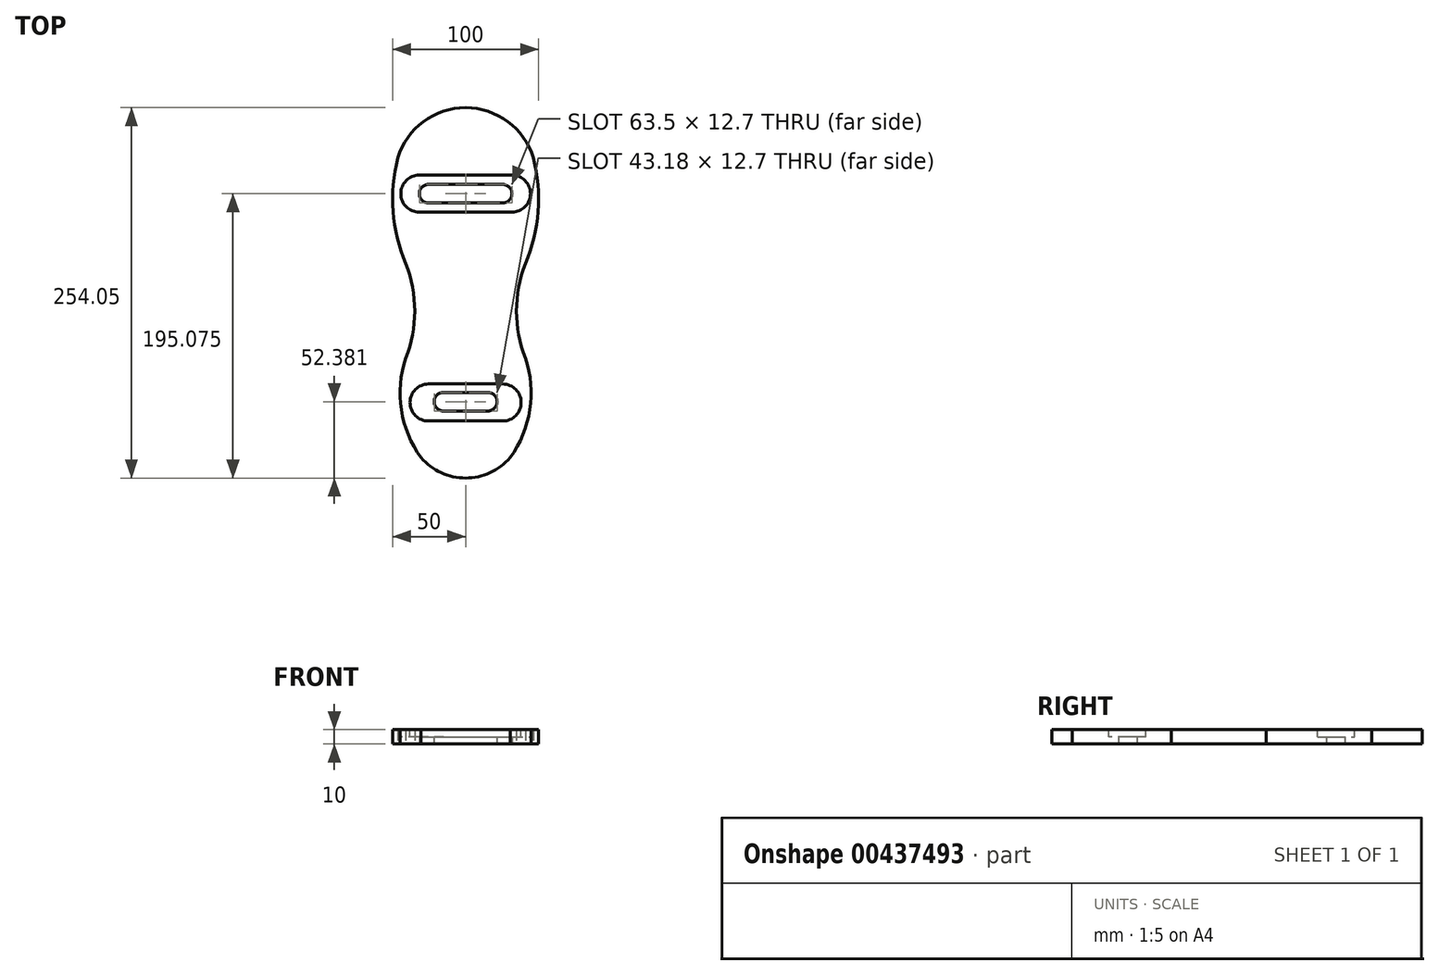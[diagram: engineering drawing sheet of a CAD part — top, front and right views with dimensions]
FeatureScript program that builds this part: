
annotation { "Feature Type Name" : "Feature", "Feature Type Description" : "" }
export const myFeature = defineFeature(function(context is Context, id is Id, definition is map)
    precondition{}
    {
        {
            var Q0;
            Q0=qCreatedBy(makeId("Top.planeOp"),FACE);
            var sketch = newSketch(context, id + "F0", { "sketchPlane" : qUnion([Q0])});
            skArc(sketch, "E0", {"start": v(-46.53, 5.97) * mm, "mid": v(-49.68, -30.66) * mm, "end": v(-41.15, -66.42) * mm});
            skArc(sketch, "E1", {"start": v(-41.15, -131.35) * mm, "mid": v(-34.86, -98.88) * mm, "end": v(-41.15, -66.42) * mm});
            skArc(sketch, "E2", {"start": v(-41.15, -131.35) * mm, "mid": v(-44.1, -166.7) * mm, "end": v(-30.54, -199.47) * mm});
            skLineSegment(sketch, "E3", {"start": v(0, 0) * mm, "end": v(0, -117.28) * mm});
            skArc(sketch, "E4.MirrorCS", {"start": v(46.53, 5.97) * mm, "mid": v(49.68, -30.66) * mm, "end": v(41.15, -66.42) * mm});
            skArc(sketch, "E5.MirrorCS", {"start": v(41.15, -131.35) * mm, "mid": v(34.86, -98.88) * mm, "end": v(41.15, -66.42) * mm});
            skArc(sketch, "E6.MirrorCS", {"start": v(41.15, -131.35) * mm, "mid": v(44.1, -166.7) * mm, "end": v(30.54, -199.47) * mm});
            skArc(sketch, "E7", {"start": v(-30.54, -199.47) * mm, "mid": v(0, -213.5) * mm, "end": v(30.54, -199.47) * mm});
            skArc(sketch, "E8", {"start": v(46.53, 5.97) * mm, "mid": v(0, 40.56) * mm, "end": v(-46.53, 5.97) * mm});
            skSolve(sketch);
        }
        {
            var Q0;
            Q0=makeQuery(id+"F0.imprint","IMPRINT",FACE,{"disambiguationData":[TD([[makeQuery(id+"F0.imprint","IMPRINT",EDGE,{"derivedFrom":sQuery(id+"F0.wireOp",EDGE,"E0")}),1.0]])]});
            extrude(context, id + "F1", {"entities" : qUnion([Q0]), "depth" : 10 * mm});
        }
        {
            var Q0;
            Q0=makeQuery(id+"F1.opExtrude","CAP_FACE",FACE,{"disambiguationData":[OSD([sQuery(id+"F0.wireOp",EDGE,"E0"),sQuery(id+"F0.wireOp",EDGE,"E1"),sQuery(id+"F0.wireOp",EDGE,"E2"),sQuery(id+"F0.wireOp",EDGE,"E4.MirrorCS"),sQuery(id+"F0.wireOp",EDGE,"E5.MirrorCS"),sQuery(id+"F0.wireOp",EDGE,"E6.MirrorCS"),sQuery(id+"F0.wireOp",EDGE,"E7"),sQuery(id+"F0.wireOp",EDGE,"E8")])],"isStart":false});
            var sketch = newSketch(context, id + "F2", { "sketchPlane" : qUnion([Q0])});
            skLineSegment(sketch, "E9", {"start": v(0, 0) * mm, "end": v(0, -18.41) * mm});
            skLineSegment(sketch, "E10", {"start": v(0, -18.41) * mm, "end": v(-31.75, -18.41) * mm});
            skCircle(sketch, "E11", {"center": v(-31.75, -18.41) * mm, "radius": 12.7 * mm});
            skCircle(sketch, "E12.MirrorC", {"center": v(31.75, -18.41) * mm, "radius": 12.7 * mm});
            skLineSegment(sketch, "E13", {"start": v(-31.75, -5.71) * mm, "end": v(31.75, -5.71) * mm});
            skLineSegment(sketch, "E14", {"start": v(31.75, -31.12) * mm, "end": v(-31.75, -31.12) * mm});
            skSolve(sketch);
        }
        {
            var Q0;
            Q0 = qSketchRegion(id + "F2", true);
            extrude(context, id + "F3", {"entities" : qUnion([Q0]), "operationType" : NewBodyOperationType.REMOVE, "oppositeDirection" : true, "depth" : 5 * mm});
        }
        {
            var Q0;
            Q0=makeQuery(id+"F3.boolean.opBoolean","COPY",FACE,{"derivedFrom":makeQuery(id+"F3.opExtrude","CAP_FACE",FACE,{"disambiguationData":[OSD([sQuery(id+"F2.wireOp",EDGE,"E11"),sQuery(id+"F2.wireOp",EDGE,"E12.MirrorC"),sQuery(id+"F2.wireOp",EDGE,"E13"),sQuery(id+"F2.wireOp",EDGE,"E14")])],"isStart":false})});
            var sketch = newSketch(context, id + "F4", { "sketchPlane" : qUnion([Q0])});
            skLineSegment(sketch, "E15", {"start": v(-31.75, -18.41) * mm, "end": v(-31.75, -12.06) * mm});
            skLineSegment(sketch, "E16", {"start": v(-31.75, -12.06) * mm, "end": v(31.75, -12.06) * mm});
            skLineSegment(sketch, "E17", {"start": v(31.75, -12.06) * mm, "end": v(31.75, -24.76) * mm});
            skLineSegment(sketch, "E18", {"start": v(31.75, -24.76) * mm, "end": v(-31.75, -24.76) * mm});
            skLineSegment(sketch, "E19", {"start": v(-31.75, -24.76) * mm, "end": v(-31.75, -18.41) * mm});
            skSolve(sketch);
        }
        {
            var Q0;
            Q0 = qSketchRegion(id + "F4", true);
            extrude(context, id + "F5", {"entities" : qUnion([Q0]), "operationType" : NewBodyOperationType.REMOVE, "oppositeDirection" : true, "depth" : 25.4 * mm});
        }
        {
            var Q0;
            Q0=makeQuery(id+"F5.boolean.opBoolean","COPY",EDGE,{"derivedFrom":makeQuery(id+"F5.opExtrude","SWEPT_EDGE",EDGE,{"disambiguationData":[OSD([sQuery(id+"F4.wireOp",EDGE,"E15"),sQuery(id+"F4.wireOp",EDGE,"E16")])]})});
            var Q1;
            Q1=makeQuery(id+"F5.boolean.opBoolean","COPY",EDGE,{"derivedFrom":makeQuery(id+"F5.opExtrude","SWEPT_EDGE",EDGE,{"disambiguationData":[OSD([sQuery(id+"F4.wireOp",EDGE,"E18"),sQuery(id+"F4.wireOp",EDGE,"E19")])]})});
            var Q2;
            Q2=makeQuery(id+"F5.boolean.opBoolean","COPY",EDGE,{"derivedFrom":makeQuery(id+"F5.opExtrude","SWEPT_EDGE",EDGE,{"disambiguationData":[OSD([sQuery(id+"F4.wireOp",EDGE,"E16"),sQuery(id+"F4.wireOp",EDGE,"E17")])]})});
            var Q3;
            Q3=makeQuery(id+"F5.boolean.opBoolean","COPY",EDGE,{"derivedFrom":makeQuery(id+"F5.opExtrude","SWEPT_EDGE",EDGE,{"disambiguationData":[OSD([sQuery(id+"F4.wireOp",EDGE,"E17"),sQuery(id+"F4.wireOp",EDGE,"E18")])]})});
            fillet(context, id + "F6", {"entities" : qUnion([Q0, Q1, Q2, Q3]), "radius" : 6.35 * mm, "tangentPropagation" : true, "allowEdgeOverflow" : false});
        }
        {
            var Q0;
            Q0=makeQuery(id+"F1.opExtrude","CAP_FACE",FACE,{"disambiguationData":[OSD([sQuery(id+"F0.wireOp",EDGE,"E0"),sQuery(id+"F0.wireOp",EDGE,"E1"),sQuery(id+"F0.wireOp",EDGE,"E2"),sQuery(id+"F0.wireOp",EDGE,"E4.MirrorCS"),sQuery(id+"F0.wireOp",EDGE,"E5.MirrorCS"),sQuery(id+"F0.wireOp",EDGE,"E6.MirrorCS"),sQuery(id+"F0.wireOp",EDGE,"E7"),sQuery(id+"F0.wireOp",EDGE,"E8")])],"isStart":false});
            var sketch = newSketch(context, id + "F7", { "sketchPlane" : qUnion([Q0])});
            skPoint(sketch, "E20.endSnap0", {"position": v(0, -5.71) * mm});
            skLineSegment(sketch, "E21", {"start": v(-25.4, -149) * mm, "end": v(25.4, -149) * mm});
            skLineSegment(sketch, "E22", {"start": v(25.4, -174.4) * mm, "end": v(-25.4, -174.4) * mm});
            skArc(sketch, "E23", {"start": v(-15.24, -154.76) * mm, "mid": v(-21.59, -161.1) * mm, "end": v(-15.24, -167.46) * mm});
            skArc(sketch, "E24", {"start": v(15.24, -167.46) * mm, "mid": v(21.6, -161.1) * mm, "end": v(15.24, -154.76) * mm});
            skLineSegment(sketch, "E25", {"start": v(-15.24, -154.76) * mm, "end": v(15.24, -154.76) * mm});
            skLineSegment(sketch, "E26", {"start": v(15.24, -167.46) * mm, "end": v(-15.24, -167.46) * mm});
            skPoint(sketch, "E27.start.orphan", {"position": v(0, -161.1) * mm});
            skPoint(sketch, "E28.trimOffspring.end.orphan", {"position": v(0, -173.23) * mm});
            skArc(sketch, "E29", {"start": v(-25.4, -149) * mm, "mid": v(-38.1, -161.7) * mm, "end": v(-25.4, -174.4) * mm});
            skArc(sketch, "E30.trimOffspring", {"start": v(25.4, -174.4) * mm, "mid": v(38.1, -161.7) * mm, "end": v(25.4, -149) * mm});
            skPoint(sketch, "E31.start.orphan", {"position": v(0, -149) * mm});
            skPoint(sketch, "E32.end.orphan", {"position": v(-25.4, -168.04) * mm});
            skSolve(sketch);
        }
        {
            var Q0;
            Q0 = qSketchRegion(id + "F7", true);
            extrude(context, id + "F8", {"entities" : qUnion([Q0]), "operationType" : NewBodyOperationType.REMOVE, "oppositeDirection" : true, "depth" : 5 * mm, "offsetDistance" : 25.4 * mm});
        }
        {
            var Q0;
            Q0=makeQuery(id+"F8.boolean.opBoolean","SPLIT",FACE,{"disambiguationData":[TD([makeQuery(id+"F8.opExtrude","SWEPT_FACE",FACE,{"disambiguationData":[OSD([sQuery(id+"F7.wireOp",EDGE,"E23")])]})])],"derivedFrom":makeQuery(id+"F1.opExtrude","CAP_FACE",FACE,{"disambiguationData":[OSD([sQuery(id+"F0.wireOp",EDGE,"E0"),sQuery(id+"F0.wireOp",EDGE,"E1"),sQuery(id+"F0.wireOp",EDGE,"E2"),sQuery(id+"F0.wireOp",EDGE,"E4.MirrorCS"),sQuery(id+"F0.wireOp",EDGE,"E5.MirrorCS"),sQuery(id+"F0.wireOp",EDGE,"E6.MirrorCS"),sQuery(id+"F0.wireOp",EDGE,"E7"),sQuery(id+"F0.wireOp",EDGE,"E8")])],"isStart":false})});
            extrude(context, id + "F9", {"entities" : qUnion([Q0]), "operationType" : NewBodyOperationType.REMOVE, "oppositeDirection" : true, "depth" : 25.4 * mm, "offsetDistance" : 25.4 * mm});
        }
    });
